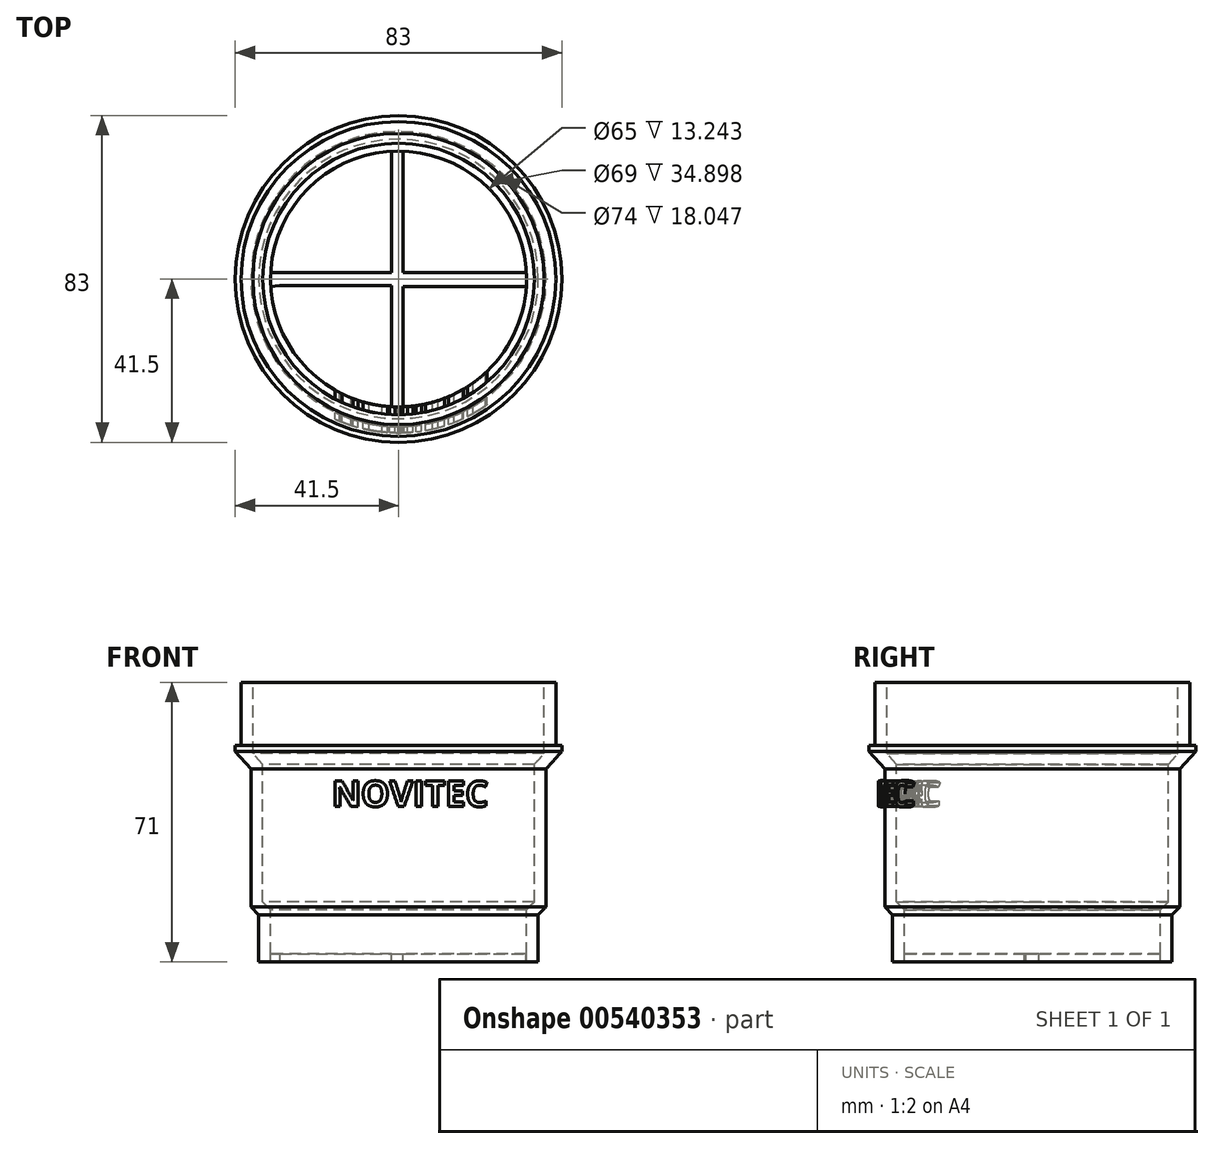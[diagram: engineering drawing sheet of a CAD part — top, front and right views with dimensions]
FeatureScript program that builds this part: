
annotation { "Feature Type Name" : "Feature", "Feature Type Description" : "" }
export const myFeature = defineFeature(function(context is Context, id is Id, definition is map)
    precondition{}
    {
        {
            var Q0;
            Q0=qCreatedBy(makeId("Front.planeOp"),FACE);
            var sketch = newSketch(context, id + "F0", { "sketchPlane" : qUnion([Q0])});
            skLineSegment(sketch, "E0", {"start": v(0, 30.69) * mm, "end": v(0, -7.89) * mm, "construction": true});
            skLineSegment(sketch, "E1", {"start": v(35.5, 0) * mm, "end": v(35.5, 12) * mm});
            skLineSegment(sketch, "E2", {"start": v(35.5, 12) * mm, "end": v(37.5, 14) * mm});
            skLineSegment(sketch, "E3", {"start": v(37.5, 14) * mm, "end": v(37.5, 49) * mm});
            skLineSegment(sketch, "E4", {"start": v(37.5, 49) * mm, "end": v(41.5, 53.5) * mm});
            skLineSegment(sketch, "E5", {"start": v(41.5, 53.5) * mm, "end": v(41.5, 55) * mm});
            skLineSegment(sketch, "E6", {"start": v(41.5, 55) * mm, "end": v(40, 55) * mm});
            skLineSegment(sketch, "E7", {"start": v(40, 55) * mm, "end": v(40, 71) * mm});
            skLineSegment(sketch, "E8.0", {"start": v(37, 52.95) * mm, "end": v(37, 71) * mm});
            skLineSegment(sketch, "E8.1", {"start": v(32.5, 0) * mm, "end": v(32.5, 13.24) * mm});
            skLineSegment(sketch, "E8.2", {"start": v(32.5, 13.24) * mm, "end": v(34.5, 15.24) * mm});
            skLineSegment(sketch, "E8.3", {"start": v(34.5, 15.24) * mm, "end": v(34.5, 50.14) * mm});
            skLineSegment(sketch, "E8.4", {"start": v(34.5, 50.14) * mm, "end": v(37, 52.95) * mm});
            skLineSegment(sketch, "E9", {"start": v(40, 71) * mm, "end": v(37, 71) * mm});
            skLineSegment(sketch, "E10", {"start": v(35.5, 0) * mm, "end": v(32.5, 0) * mm});
            skSolve(sketch);
        }
        {
            var Q0;
            Q0=makeQuery(id+"F0.imprint","IMPRINT",FACE,{"disambiguationData":[TD([[makeQuery(id+"F0.imprint","IMPRINT",EDGE,{"derivedFrom":sQuery(id+"F0.wireOp",EDGE,"E1")}),1.0]])]});
            var Q1;
            Q1=sQuery(id+"F0.wireOp",EDGE,"E0");
            revolve(context, id + "F1", {"entities" : qUnion([Q0]), "axis" : qUnion([Q1]), "revolveType" : RevolveType.FULL});
        }
        {
            var Q0;
            Q0=qCreatedBy(makeId("Front.planeOp"),FACE);
            var sketch = newSketch(context, id + "F2", { "sketchPlane" : qUnion([Q0])});
            skText(sketch, "E11", { "text": "NOVITEC", "fontName": "OpenSans-Bold.ttf"});
            const initialGuessF2  = {"E11": [-0.0169, 0.03945, 1, 0, 0.00655]};
            skSetInitialGuess(sketch, initialGuessF2);
            skSolve(sketch);
        }
        {
            var Q0;
            Q0 = qSketchRegion(id + "F2", true);
            extrude(context, id + "F3", {"entities" : qUnion([Q0]), "operationType" : NewBodyOperationType.ADD, "depth" : 80 * mm, "offsetDistance" : 25 * mm});
        }
        {
            var Q0;
            Q0=makeQuery(id+"F1.opRevolve","SWEPT_FACE",FACE,{"disambiguationData":[OSD([sQuery(id+"F0.wireOp",EDGE,"E10")])]});
            var sketch = newSketch(context, id + "F4", { "sketchPlane" : qUnion([Q0])});
            skSolve(sketch);
        }
        {
            var Q0;
            Q0=makeQuery(id+"F4.imprint","IMPRINT",FACE,{"disambiguationData":[TD([[makeQuery(id+"F4.imprint","IMPRINT",EDGE,{"derivedFrom":makeQuery(id+"F1.opRevolve","SWEPT_EDGE",EDGE,{"disambiguationData":[OSD([sQuery(id+"F0.wireOp",EDGE,"E8.1"),sQuery(id+"F0.wireOp",EDGE,"E10")])]})}),-1.0]])]});
            extrude(context, id + "F5", {"entities" : qUnion([Q0]), "operationType" : NewBodyOperationType.REMOVE, "endBound" : BoundingType.THROUGH_ALL, "oppositeDirection" : true, "depth" : 25 * mm, "offsetDistance" : 25 * mm});
        }
        {
            var Q0;
            Q0=makeQuery(id+"F1.opRevolve","SWEPT_FACE",FACE,{"disambiguationData":[OSD([sQuery(id+"F0.wireOp",EDGE,"E10")])]});
            var sketch = newSketch(context, id + "F6", { "sketchPlane" : qUnion([Q0])});
            skCircle(sketch, "E12", {"center": v(0, 0) * mm, "radius": 39.08 * mm});
            skCircle(sketch, "E13", {"center": v(1.25, 0) * mm, "radius": 93.1 * mm});
            skSolve(sketch);
        }
        {
            var Q0;
            Q0 = qSketchRegion(id + "F6", true);
            extrude(context, id + "F7", {"entities" : qUnion([Q0]), "operationType" : NewBodyOperationType.REMOVE, "oppositeDirection" : true, "depth" : 47.3 * mm, "offsetDistance" : 25 * mm});
        }
        {
            var Q0;
            Q0=makeQuery(id+"F1.opRevolve","SWEPT_FACE",FACE,{"disambiguationData":[OSD([sQuery(id+"F0.wireOp",EDGE,"E10")])]});
            var sketch = newSketch(context, id + "F8", { "sketchPlane" : qUnion([Q0])});
            skLineSegment(sketch, "E14", {"start": v(-30.2, 1.73) * mm, "end": v(-1.73, 1.73) * mm});
            skLineSegment(sketch, "E15", {"start": v(-1.73, 1.73) * mm, "end": v(-1.73, 30.93) * mm});
            skLineSegment(sketch, "E16", {"start": v(-1.73, 30.93) * mm, "end": v(1.1, 30.93) * mm});
            skLineSegment(sketch, "E17", {"start": v(1.1, 30.93) * mm, "end": v(1.1, 1.97) * mm});
            skLineSegment(sketch, "E18", {"start": v(1.1, 1.97) * mm, "end": v(30.8, 1.97) * mm});
            skLineSegment(sketch, "E19", {"start": v(30.8, 1.97) * mm, "end": v(34.38, 1.97) * mm});
            skLineSegment(sketch, "E20", {"start": v(34.38, 1.97) * mm, "end": v(34.38, -1.6) * mm});
            skLineSegment(sketch, "E21", {"start": v(34.38, -1.6) * mm, "end": v(1.1, -1.6) * mm});
            skLineSegment(sketch, "E22", {"start": v(1.1, -1.6) * mm, "end": v(1.1, -33.52) * mm});
            skLineSegment(sketch, "E23", {"start": v(1.1, -33.52) * mm, "end": v(-1.73, -33.52) * mm});
            skLineSegment(sketch, "E24", {"start": v(-1.73, -33.52) * mm, "end": v(-1.73, -1.6) * mm});
            skLineSegment(sketch, "E25", {"start": v(-1.73, -1.6) * mm, "end": v(-33.77, -1.6) * mm});
            skLineSegment(sketch, "E26", {"start": v(-33.77, -1.6) * mm, "end": v(-33.77, 1.97) * mm});
            skLineSegment(sketch, "E27", {"start": v(-33.77, 1.97) * mm, "end": v(-30.2, 1.73) * mm});
            skLineSegment(sketch, "E28", {"start": v(-1.73, 30.93) * mm, "end": v(-1.73, 32.45) * mm});
            skLineSegment(sketch, "E29", {"start": v(-1.73, 32.45) * mm, "end": v(-1.73, 34.14) * mm});
            skLineSegment(sketch, "E30", {"start": v(-1.73, 34.14) * mm, "end": v(1.1, 34.14) * mm});
            skLineSegment(sketch, "E31", {"start": v(1.1, 34.14) * mm, "end": v(1.1, 30.93) * mm});
            skSolve(sketch);
        }
        {
            var Q0;
            {var subQ15=sQuery(id+"F8.wireOp",EDGE,"E14");Q0=makeQuery(id+"F8.imprint","IMPRINT",FACE,{"disambiguationData":[TD([[makeQuery(id+"F8.imprint","IMPRINT",EDGE,{"derivedFrom":subQ15}),-1.0]])]});}
            var Q1;
            {var subQ0=sQuery(id+"F8.wireOp",EDGE,"E26");Q1=makeQuery(id+"F8.imprint","IMPRINT",FACE,{"disambiguationData":[TD([[makeQuery(id+"F8.imprint","IMPRINT",EDGE,{"derivedFrom":subQ0}),-1.0]])]});}
            var Q2;
            {var subQ0=sQuery(id+"F8.wireOp",EDGE,"E16");Q2=makeQuery(id+"F8.imprint","IMPRINT",FACE,{"disambiguationData":[TD([[makeQuery(id+"F8.imprint","IMPRINT",EDGE,{"derivedFrom":subQ0}),1.0]])]});}
            var Q3;
            {var subQ0=sQuery(id+"F8.wireOp",EDGE,"E29");Q3=makeQuery(id+"F8.imprint","IMPRINT",FACE,{"disambiguationData":[TD([[makeQuery(id+"F8.imprint","IMPRINT",EDGE,{"derivedFrom":subQ0}),-1.0]])]});}
            var Q4;
            {var subQ0=sQuery(id+"F8.wireOp",EDGE,"E20");Q4=makeQuery(id+"F8.imprint","IMPRINT",FACE,{"disambiguationData":[TD([[makeQuery(id+"F8.imprint","IMPRINT",EDGE,{"derivedFrom":subQ0}),-1.0]])]});}
            var Q5;
            {var subQ0=sQuery(id+"F8.wireOp",EDGE,"E23");Q5=makeQuery(id+"F8.imprint","IMPRINT",FACE,{"disambiguationData":[TD([[makeQuery(id+"F8.imprint","IMPRINT",EDGE,{"derivedFrom":subQ0}),-1.0]])]});}
            extrude(context, id + "F9", {"entities" : qUnion([Q0, Q1, Q2, Q3, Q4, Q5]), "operationType" : NewBodyOperationType.ADD, "oppositeDirection" : true, "depth" : 2 * mm, "offsetDistance" : 25 * mm});
        }
    });
